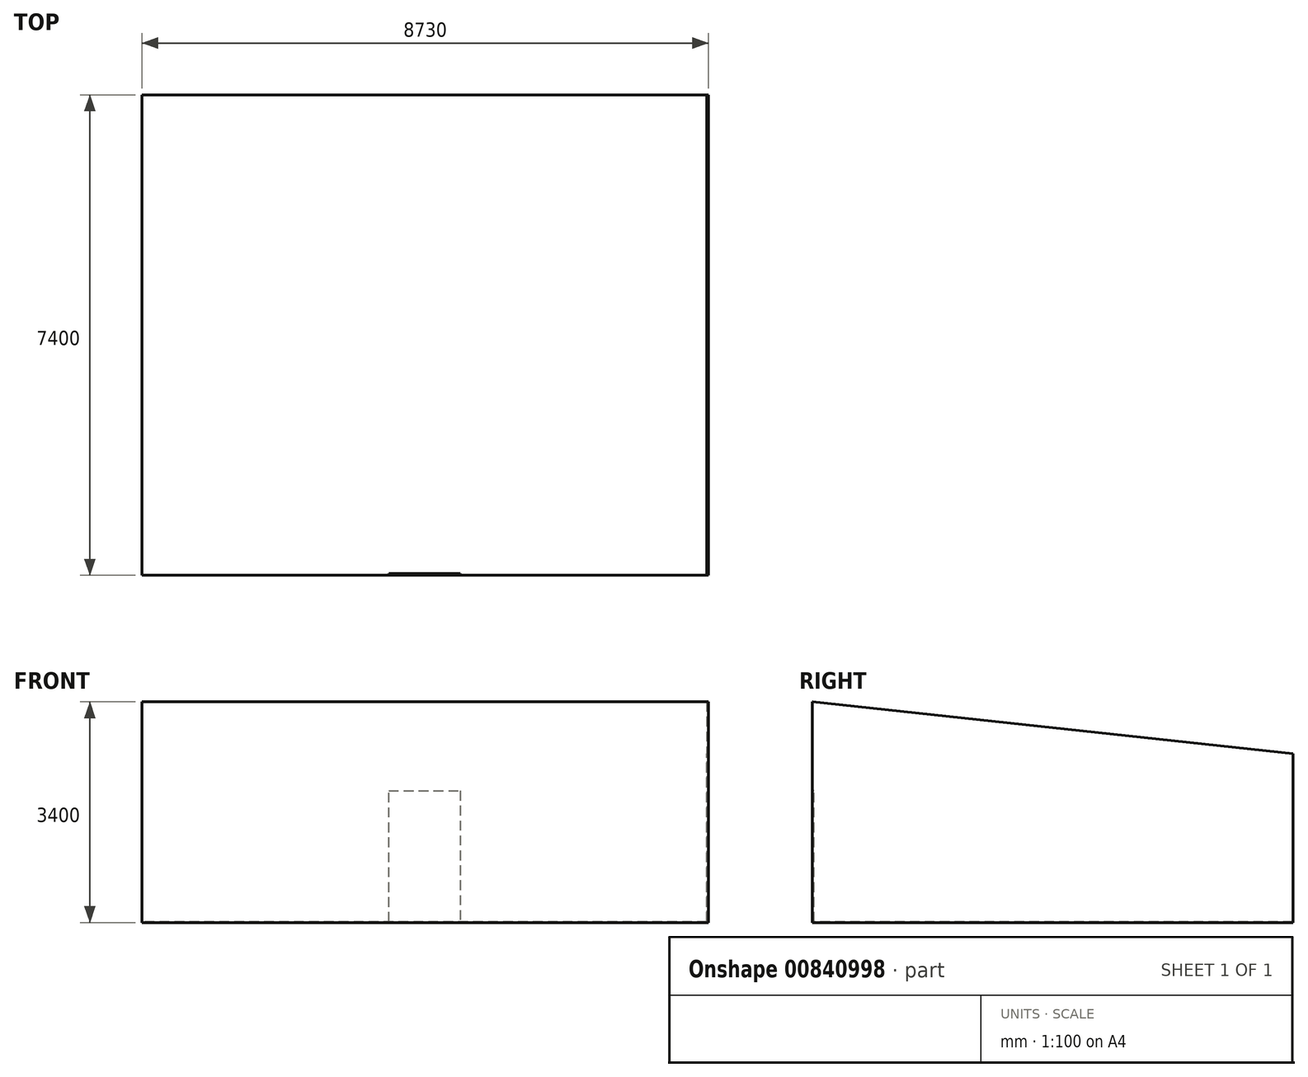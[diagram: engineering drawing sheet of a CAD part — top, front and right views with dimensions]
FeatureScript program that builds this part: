
annotation { "Feature Type Name" : "Feature", "Feature Type Description" : "" }
export const myFeature = defineFeature(function(context is Context, id is Id, definition is map)
    precondition{}
    {
        {
            var Q0;
            Q0=qCreatedBy(makeId("Top.planeOp"),FACE);
            var sketch = newSketch(context, id + "F0", { "sketchPlane" : qUnion([Q0])});
            skLineSegment(sketch, "E0.bottom", {"start": v(4350, 3700) * mm, "end": v(-4350, 3700) * mm});
            skLineSegment(sketch, "E0.top", {"start": v(4350, -3700) * mm, "end": v(-4350, -3700) * mm});
            skLineSegment(sketch, "E0.left", {"start": v(4350, 3700) * mm, "end": v(4350, -3700) * mm});
            skLineSegment(sketch, "E0.right", {"start": v(-4350, 3700) * mm, "end": v(-4350, -3700) * mm});
            skPoint(sketch, "E0.middle", {"position": v(0, 0) * mm});
            skLineSegment(sketch, "E1", {"start": v(0, 0) * mm, "end": v(0, -3700) * mm, "construction": true});
            skLineSegment(sketch, "E2", {"start": v(0, 0) * mm, "end": v(-4350, 0) * mm, "construction": true});
            skSolve(sketch);
        }
        {
            var Q0;
            Q0=sQuery(id+"F0.wireOp",EDGE,"E0.top");
            cPlane(context, id + "F1", {"entities" : qUnion([Q0]), "cplaneType" : CPlaneType.LINE_ANGLE, "offset" : 25 * mm, "angle" : 0 * degree, "width" : 150 * mm, "height" : 150 * mm});
        }
        {
            var Q0;
            Q0=qCreatedBy(id+"F1.planeOp",FACE);
            var sketch = newSketch(context, id + "F2", { "sketchPlane" : qUnion([Q0])});
            skLineSegment(sketch, "E3", {"start": v(-4350, 0) * mm, "end": v(-4350, 3400) * mm});
            skLineSegment(sketch, "E4", {"start": v(4350, 3400) * mm, "end": v(4350, 0) * mm});
            skLineSegment(sketch, "E5", {"start": v(-4350, 3400) * mm, "end": v(4350, 3400) * mm});
            skLineSegment(sketch, "E6", {"start": v(4350, 0) * mm, "end": v(-4350, 0) * mm});
            skSolve(sketch);
        }
        {
            var Q0;
            Q0=sQuery(id+"F0.wireOp",EDGE,"E0.bottom");
            cPlane(context, id + "F3", {"entities" : qUnion([Q0]), "cplaneType" : CPlaneType.LINE_ANGLE, "offset" : 25 * mm, "angle" : 0 * degree, "width" : 150 * mm, "height" : 150 * mm});
        }
        {
            var Q0;
            Q0=qCreatedBy(id+"F3.planeOp",FACE);
            var sketch = newSketch(context, id + "F4", { "sketchPlane" : qUnion([Q0])});
            skLineSegment(sketch, "E7", {"start": v(4350, 0) * mm, "end": v(4350, 2600) * mm});
            skLineSegment(sketch, "E8", {"start": v(-4350, 0) * mm, "end": v(-4350, 2600) * mm});
            skLineSegment(sketch, "E9", {"start": v(4350, 2600) * mm, "end": v(-4350, 2600) * mm});
            skSolve(sketch);
        }
        {
            var Q0;
            Q0=sQuery(id+"F0.wireOp",EDGE,"E0.left");
            cPlane(context, id + "F5", {"entities" : qUnion([Q0]), "cplaneType" : CPlaneType.LINE_ANGLE, "offset" : 25 * mm, "angle" : 90 * degree, "width" : 150 * mm, "height" : 150 * mm});
        }
        {
            var Q0;
            Q0=qCreatedBy(id+"F5.planeOp",FACE);
            var sketch = newSketch(context, id + "F6", { "sketchPlane" : qUnion([Q0])});
            skLineSegment(sketch, "E10.bottom", {"start": v(-3700, 0) * mm, "end": v(3700, 0) * mm});
            skLineSegment(sketch, "E10.top", {"start": v(-3700, 3400) * mm, "end": v(3700, 2600) * mm});
            skLineSegment(sketch, "E10.left", {"start": v(-3700, 0) * mm, "end": v(-3700, 3419.81) * mm});
            skLineSegment(sketch, "E10.right", {"start": v(3700, 0) * mm, "end": v(3700, 2600) * mm});
            skSolve(sketch);
        }
        {
            var Q0;
            {var subQ0=sQuery(id+"F6.wireOp",EDGE,"E10.bottom");Q0=makeQuery(id+"F6.imprint","IMPRINT",FACE,{"disambiguationData":[TD([[makeQuery(id+"F6.imprint","IMPRINT",EDGE,{"derivedFrom":subQ0}),1.0]])]});}
            extrude(context, id + "F7", {"entities" : qUnion([Q0]), "depth" : 25 * mm, "offsetDistance" : 25 * mm});
        }
        {
            var Q0;
            Q0 = qSketchRegion(id + "F0", true);
            extrude(context, id + "F8", {"entities" : qUnion([Q0]), "operationType" : NewBodyOperationType.ADD, "depth" : 10 * mm, "offsetDistance" : 25 * mm});
        }
        {
            var Q0;
            Q0=makeQuery(id+"F2.imprint","IMPRINT",FACE,{"disambiguationData":[TD([[makeQuery(id+"F2.imprint","IMPRINT",EDGE,{"derivedFrom":sQuery(id+"F2.wireOp",EDGE,"E3")}),-1.0]])]});
            extrude(context, id + "F9", {"entities" : qUnion([Q0]), "operationType" : NewBodyOperationType.ADD, "oppositeDirection" : true, "depth" : 1 * mm, "offsetDistance" : 25 * mm});
        }
        {
            var Q0;
            Q0=makeQuery(id+"F8.opExtrude","CAP_EDGE",EDGE,{"disambiguationData":[OSD([sQuery(id+"F0.wireOp",EDGE,"E0.right")])],"isStart":false});
            cPlane(context, id + "F10", {"entities" : qUnion([Q0]), "cplaneType" : CPlaneType.LINE_ANGLE, "offset" : 25 * mm, "angle" : 90 * degree, "width" : 150 * mm, "height" : 150 * mm});
        }
        {
            var Q0;
            Q0=qCreatedBy(id+"F10.planeOp",FACE);
            var sketch = newSketch(context, id + "F11", { "sketchPlane" : qUnion([Q0])});
            skLineSegment(sketch, "E11.bottom", {"start": v(-3700, 0) * mm, "end": v(3700, 0) * mm});
            skLineSegment(sketch, "E11.top", {"start": v(-3700, 3400) * mm, "end": v(3700, 2600) * mm});
            skLineSegment(sketch, "E11.left", {"start": v(-3700, 0) * mm, "end": v(-3700, 3419.81) * mm});
            skLineSegment(sketch, "E11.right", {"start": v(3700, 0) * mm, "end": v(3700, 2600) * mm});
            skLineSegment(sketch, "E12", {"start": v(3200, 0) * mm, "end": v(3200, 800) * mm, "construction": true});
            skLineSegment(sketch, "E13", {"start": v(3200, 800) * mm, "end": v(3700, 800) * mm, "construction": true});
            skSolve(sketch);
        }
        {
            var Q0;
            {var subQ0=sQuery(id+"F11.wireOp",EDGE,"E11.bottom");Q0=makeQuery(id+"F11.imprint","IMPRINT",FACE,{"disambiguationData":[TD([[makeQuery(id+"F11.imprint","IMPRINT",EDGE,{"derivedFrom":subQ0}),1.0]])]});}
            var Q1;
            Q1 = qConstructionFilter(qBodyType(qCreatedBy(id + "F11" ,EDGE), BodyType.WIRE), ConstructionObject.NO);
            extrude(context, id + "F12", {"entities" : qUnion([Q0]), "operationType" : NewBodyOperationType.ADD, "surfaceEntities" : qUnion([Q1]), "oppositeDirection" : true, "depth" : 5 * mm, "offsetDistance" : 25 * mm});
        }
        {
            var Q0;
            Q0=makeQuery(id+"F2.imprint","IMPRINT",FACE,{"disambiguationData":[TD([[makeQuery(id+"F2.imprint","IMPRINT",EDGE,{"derivedFrom":sQuery(id+"F2.wireOp",EDGE,"E3")}),-1.0]])]});
            var sketch = newSketch(context, id + "F13", { "sketchPlane" : qUnion([Q0])});
            skLineSegment(sketch, "E14", {"start": v(-550, 0) * mm, "end": v(550, 0) * mm});
            skLineSegment(sketch, "E15", {"start": v(-550, 0) * mm, "end": v(-550, 2029.17) * mm});
            skLineSegment(sketch, "E16", {"start": v(-550, 2029.17) * mm, "end": v(550, 2029.17) * mm});
            skLineSegment(sketch, "E17", {"start": v(550, 2029.17) * mm, "end": v(550, 0) * mm});
            skSolve(sketch);
        }
        {
            var Q0;
            Q0 = qSketchRegion(id + "F13", true);
            extrude(context, id + "F14", {"entities" : qUnion([Q0]), "operationType" : NewBodyOperationType.ADD, "oppositeDirection" : true, "depth" : 25 * mm, "offsetDistance" : 25 * mm});
        }
    });
